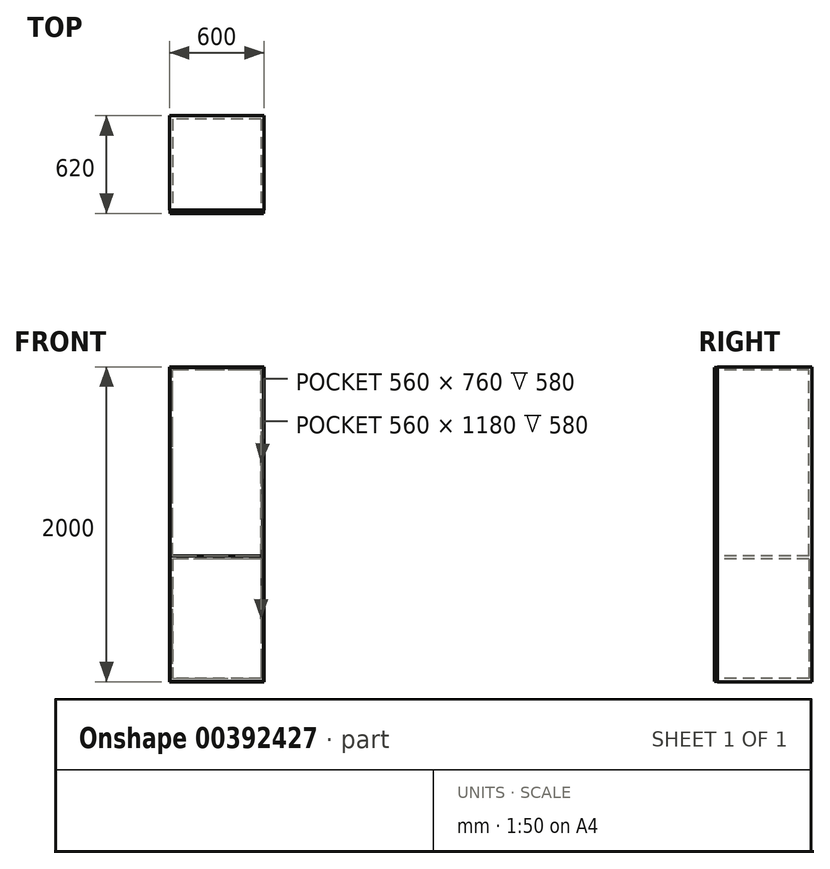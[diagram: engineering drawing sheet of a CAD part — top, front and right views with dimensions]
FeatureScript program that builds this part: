
annotation { "Feature Type Name" : "Feature", "Feature Type Description" : "" }
export const myFeature = defineFeature(function(context is Context, id is Id, definition is map)
    precondition{}
    {
        {
            var Q0;
            Q0=qCreatedBy(makeId("Top.planeOp"),FACE);
            var sketch = newSketch(context, id + "F0", { "sketchPlane" : qUnion([Q0])});
            skLineSegment(sketch, "E0", {"start": v(1706.36, 1150.45) * mm, "end": v(-1723.64, 1150.45) * mm});
            skLineSegment(sketch, "E1", {"start": v(1741.54, -774.13) * mm, "end": v(1706.36, 1150.45) * mm});
            skLineSegment(sketch, "E2", {"start": v(1741.54, -774.13) * mm, "end": v(-1723.64, -774.13) * mm});
            skLineSegment(sketch, "E3", {"start": v(-1723.64, 1150.45) * mm, "end": v(-1723.64, -774.13) * mm});
            skPoint(sketch, "E4", {"position": v(-1723.64, -774.13) * mm});
            skSolve(sketch);
        }
        {
            var Q0;
            Q0=makeQuery(id+"F0.imprint","IMPRINT",FACE,{"disambiguationData":[TD([[makeQuery(id+"F0.imprint","IMPRINT",EDGE,{"derivedFrom":sQuery(id+"F0.wireOp",EDGE,"E0")}),1.0]])]});
            var sketch = newSketch(context, id + "F1", { "sketchPlane" : qUnion([Q0])});
            skLineSegment(sketch, "E5.bottom", {"start": v(1706.36, 1150.45) * mm, "end": v(1106.36, 1150.45) * mm});
            skLineSegment(sketch, "E5.top", {"start": v(1706.36, 580.45) * mm, "end": v(1106.36, 580.45) * mm});
            skLineSegment(sketch, "E5.left", {"start": v(1706.36, 1150.45) * mm, "end": v(1706.36, 580.45) * mm});
            skLineSegment(sketch, "E5.right", {"start": v(1106.36, 1150.45) * mm, "end": v(1106.36, 580.45) * mm});
            skSolve(sketch);
        }
        {
            var Q0;
            Q0=makeQuery(id+"F1.imprint","IMPRINT",FACE,{"disambiguationData":[TD([[makeQuery(id+"F1.imprint","IMPRINT",EDGE,{"derivedFrom":sQuery(id+"F1.wireOp",EDGE,"E5.bottom")}),1.0]])]});
            cPlane(context, id + "F2", {"entities" : qUnion([Q0]), "cplaneType" : CPlaneType.OFFSET, "offset" : 80 * mm, "width" : 150 * mm, "height" : 150 * mm});
        }
        {
            var Q0;
            Q0=qCreatedBy(id+"F2.planeOp",FACE);
            var sketch = newSketch(context, id + "F3", { "sketchPlane" : qUnion([Q0])});
            skLineSegment(sketch, "E6.bottom", {"start": v(1706.36, 1150.45) * mm, "end": v(1106.36, 1150.45) * mm});
            skLineSegment(sketch, "E6.top", {"start": v(1706.36, 550.45) * mm, "end": v(1106.36, 550.45) * mm});
            skLineSegment(sketch, "E6.left", {"start": v(1706.36, 1150.45) * mm, "end": v(1706.36, 550.45) * mm});
            skLineSegment(sketch, "E6.right", {"start": v(1106.36, 1150.45) * mm, "end": v(1106.36, 550.45) * mm});
            skSolve(sketch);
        }
        {
            var Q0;
            Q0 = qSketchRegion(id + "F3", true);
            extrude(context, id + "F4", {"entities" : qUnion([Q0]), "depth" : 2000 * mm, "offsetDistance" : 25 * mm});
        }
        {
            var Q0;
            Q0=makeQuery(id+"F4.opExtrude","SWEPT_FACE",FACE,{"disambiguationData":[OSD([sQuery(id+"F3.wireOp",EDGE,"E6.top")])]});
            var sketch = newSketch(context, id + "F5", { "sketchPlane" : qUnion([Q0])});
            skLineSegment(sketch, "E7.bottom", {"start": v(1686.36, 880) * mm, "end": v(1126.36, 880) * mm});
            skLineSegment(sketch, "E7.top", {"start": v(1706.36, 80) * mm, "end": v(1106.36, 80) * mm});
            skLineSegment(sketch, "E7.left", {"start": v(1706.36, 880) * mm, "end": v(1706.36, 80) * mm});
            skLineSegment(sketch, "E7.right", {"start": v(1106.36, 880) * mm, "end": v(1106.36, 80) * mm});
            skLineSegment(sketch, "E8.top", {"start": v(1706.36, 2080) * mm, "end": v(1106.36, 2080) * mm});
            skLineSegment(sketch, "E8.left", {"start": v(1706.36, 880) * mm, "end": v(1706.36, 2080) * mm});
            skLineSegment(sketch, "E8.right", {"start": v(1106.36, 880) * mm, "end": v(1106.36, 2080) * mm});
            skLineSegment(sketch, "E9.0", {"start": v(1686.36, 880) * mm, "end": v(1686.36, 2060) * mm});
            skLineSegment(sketch, "E9.1", {"start": v(1686.36, 2060) * mm, "end": v(1126.36, 2060) * mm});
            skLineSegment(sketch, "E9.2", {"start": v(1126.36, 880) * mm, "end": v(1126.36, 2060) * mm});
            skLineSegment(sketch, "E10.0", {"start": v(1686.36, 860) * mm, "end": v(1126.36, 860) * mm});
            skLineSegment(sketch, "E10.1", {"start": v(1686.36, 860) * mm, "end": v(1686.36, 100) * mm});
            skLineSegment(sketch, "E10.2", {"start": v(1686.36, 100) * mm, "end": v(1126.36, 100) * mm});
            skLineSegment(sketch, "E10.3", {"start": v(1126.36, 860) * mm, "end": v(1126.36, 100) * mm});
            skSolve(sketch);
        }
        {
            var Q0;
            Q0=makeQuery(id+"F5.imprint","IMPRINT",FACE,{"disambiguationData":[TD([[makeQuery(id+"F5.imprint","IMPRINT",EDGE,{"derivedFrom":sQuery(id+"F5.wireOp",EDGE,"E7.bottom")}),-1.0]])]});
            var Q1;
            Q1=makeQuery(id+"F5.imprint","IMPRINT",FACE,{"disambiguationData":[TD([[makeQuery(id+"F5.imprint","IMPRINT",EDGE,{"derivedFrom":sQuery(id+"F5.wireOp",EDGE,"E10.0")}),1.0]])]});
            extrude(context, id + "F6", {"entities" : qUnion([Q0, Q1]), "operationType" : NewBodyOperationType.REMOVE, "oppositeDirection" : true, "depth" : 580 * mm, "offsetDistance" : 25 * mm});
        }
        {
            var Q0;
            Q0=makeQuery(id+"F4.opExtrude","SWEPT_FACE",FACE,{"disambiguationData":[OSD([sQuery(id+"F3.wireOp",EDGE,"E6.top")])]});
            var sketch = newSketch(context, id + "F7", { "sketchPlane" : qUnion([Q0])});
            skSolve(sketch);
        }
        {
            var Q0;
            {var subQ0=sQuery(id+"F3.wireOp",EDGE,"E6.top");Q0=makeQuery(id+"F7.imprint","IMPRINT",FACE,{"disambiguationData":[TD([[makeQuery(id+"F7.imprint","IMPRINT",EDGE,{"derivedFrom":makeQuery(id+"F4.opExtrude","CAP_EDGE",EDGE,{"disambiguationData":[OSD([subQ0])],"isStart":true})}),-1.0]])]});}
            cPlane(context, id + "F8", {"entities" : qUnion([Q0]), "cplaneType" : CPlaneType.OFFSET, "offset" : 0 * mm, "width" : 150 * mm, "height" : 150 * mm});
        }
        {
            var Q0;
            Q0=qCreatedBy(id+"F8.planeOp",FACE);
            var sketch = newSketch(context, id + "F9", { "sketchPlane" : qUnion([Q0])});
            skLineSegment(sketch, "E11.bottom", {"start": v(1706.36, 2080) * mm, "end": v(1106.36, 2080) * mm});
            skLineSegment(sketch, "E11.top", {"start": v(1706.36, 80) * mm, "end": v(1106.36, 80) * mm});
            skLineSegment(sketch, "E11.left", {"start": v(1706.36, 2080) * mm, "end": v(1706.36, 80) * mm});
            skLineSegment(sketch, "E11.right", {"start": v(1106.36, 2080) * mm, "end": v(1106.36, 80) * mm});
            skSolve(sketch);
        }
        {
            var Q0;
            Q0 = qSketchRegion(id + "F9", true);
            extrude(context, id + "F10", {"entities" : qUnion([Q0]), "depth" : 20 * mm, "offsetDistance" : 25 * mm});
        }
        {
            var Q0;
            Q0=makeQuery(id+"F10.opExtrude","CAP_FACE",FACE,{"disambiguationData":[OSD([sQuery(id+"F9.wireOp",EDGE,"E11.bottom"),sQuery(id+"F9.wireOp",EDGE,"E11.top"),sQuery(id+"F9.wireOp",EDGE,"E11.left"),sQuery(id+"F9.wireOp",EDGE,"E11.right")])],"isStart":false});
            var sketch = newSketch(context, id + "F11", { "sketchPlane" : qUnion([Q0])});
            skLineSegment(sketch, "E12.bottom", {"start": v(1706.36, 2080) * mm, "end": v(1106.36, 2080) * mm});
            skLineSegment(sketch, "E12.top", {"start": v(1703.86, 880) * mm, "end": v(1108.86, 880) * mm});
            skLineSegment(sketch, "E12.left", {"start": v(1706.36, 2080) * mm, "end": v(1706.36, 880) * mm});
            skLineSegment(sketch, "E12.right", {"start": v(1106.36, 2080) * mm, "end": v(1106.36, 880) * mm});
            skLineSegment(sketch, "E13.top", {"start": v(1706.36, 80) * mm, "end": v(1106.36, 80) * mm});
            skLineSegment(sketch, "E13.left", {"start": v(1706.36, 880) * mm, "end": v(1706.36, 80) * mm});
            skLineSegment(sketch, "E13.right", {"start": v(1106.36, 880) * mm, "end": v(1106.36, 80) * mm});
            skLineSegment(sketch, "E14.0", {"start": v(1108.86, 2077.5) * mm, "end": v(1108.86, 880) * mm});
            skLineSegment(sketch, "E14.1", {"start": v(1703.86, 2077.5) * mm, "end": v(1108.86, 2077.5) * mm});
            skLineSegment(sketch, "E14.2", {"start": v(1703.86, 2077.5) * mm, "end": v(1703.86, 880) * mm});
            skLineSegment(sketch, "E15.0", {"start": v(1703.86, 877.5) * mm, "end": v(1108.86, 877.5) * mm});
            skLineSegment(sketch, "E15.1", {"start": v(1703.86, 877.5) * mm, "end": v(1703.86, 82.5) * mm});
            skLineSegment(sketch, "E15.2", {"start": v(1703.86, 82.5) * mm, "end": v(1108.86, 82.5) * mm});
            skLineSegment(sketch, "E15.3", {"start": v(1108.86, 877.5) * mm, "end": v(1108.86, 82.5) * mm});
            skSolve(sketch);
        }
        {
            var Q0;
            Q0=makeQuery(id+"F11.imprint","IMPRINT",FACE,{"disambiguationData":[TD([[makeQuery(id+"F11.imprint","IMPRINT",EDGE,{"derivedFrom":sQuery(id+"F11.wireOp",EDGE,"E12.bottom")}),1.0]])]});
            extrude(context, id + "F12", {"entities" : qUnion([Q0]), "operationType" : NewBodyOperationType.REMOVE, "oppositeDirection" : true, "depth" : 20 * mm, "offsetDistance" : 25 * mm});
        }
        {
            var Q0;
            Q0=makeQuery(id+"F11.imprint","IMPRINT",FACE,{"disambiguationData":[TD([[makeQuery(id+"F11.imprint","IMPRINT",EDGE,{"derivedFrom":sQuery(id+"F11.wireOp",EDGE,"E13.top")}),-1.0]])]});
            extrude(context, id + "F13", {"entities" : qUnion([Q0]), "operationType" : NewBodyOperationType.REMOVE, "oppositeDirection" : true, "depth" : 20 * mm, "offsetDistance" : 25 * mm});
        }
    });
